# Revit family: Plumbing-Flushometer-Sloan-CX-158__
name_source: partatom
category: Plumbing Fixtures
units: mm (PartAtom-declared; Revit-internal decimal feet)

## family parameters
Cut with Voids When Loaded = No
Host = Face
Maintain Annotation Orientation = No
OmniClass Number = 23.45.05.14.99
OmniClass Title = Other Sanitary Washing Plumbing Fixtures
Part Type = Normal
Room Calculation Point = No
Round Connector Dimension = Use Diameter
Shared = No

## types (1)
- Not a Type - Load Type Catalog!
    ADA Compliant = Yes
    Assembly Code = D2020300
    CW Connection = Yes
    CWFU = 0
    Date Updated = 09.12.2024
    Default Elevation = 0"
    Description = 1.28 gpf, Filtered, Polished Chrome Finish, Fixture Connection Rear Spud, Single Flush, Integrated Control Stop, 3.25-4.25 L Dimension, Adjustable Flush Connection Outlet Tube, ADA Compliant Push Button, Short V500A & Adjustable Flush Connection Vacuum Breaker, Front Accessible Wall Box, CX Concealed Manual Water Closet Flushometer.
    Edition number = 1
    Fixture Inlet to Wall Opening = 6 1/4"
    Flush Rate = 1.28 gpf (4.8 Lpf)
    HW Connection = No
    HWFU = 0
    Height = 8 1/2"
    Keynote = 15410
    Manufacturer = Sloan Valve
    Model = Model not specified - Load type catalog!
    Operating Water Pressure = 20 – 80 PSI (138 – 552 kPa)
    Part Number = 3400201
    Product Guid = 705ad915-f848-4d48-a022-665c87b04fb2
    Product Material = Sloan Valve - Finish - Polished Chrome
    Product data url = https://bimobject.com
    URL = www.sloanvalve.com
    Valve CL to Fixture Inlet = 12 1/4"
    Valve Pressure Drop = 0.00 psi
    Vent Connection = No
    Version = 2
    WFU = 0
    Waste Connection = No
    Water Inlet Connection Diameter = 2"
    Water Outlet Connection Diameter = 2"
    Width = 7 1/2"

## geometry (parser evidence)
native form markers: Sweep x4
no freeform markers — native parametric forms only
